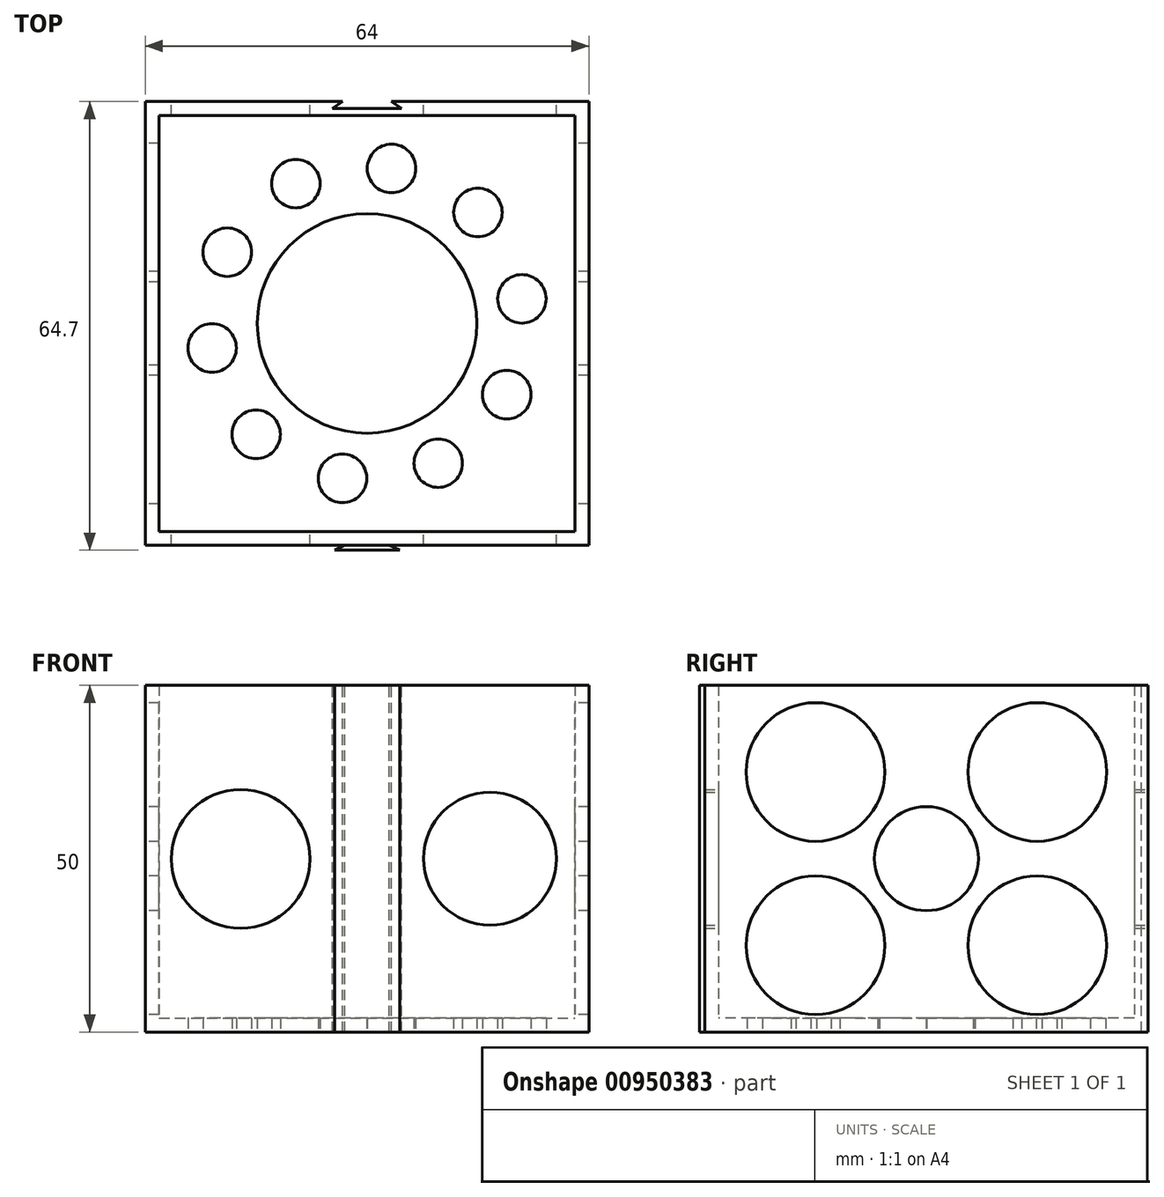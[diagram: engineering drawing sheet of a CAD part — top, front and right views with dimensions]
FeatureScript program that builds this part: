
annotation { "Feature Type Name" : "Feature", "Feature Type Description" : "" }
export const myFeature = defineFeature(function(context is Context, id is Id, definition is map)
    precondition{}
    {
        {
            var Q0;
            Q0=qCreatedBy(makeId("Top.planeOp"),FACE);
            var sketch = newSketch(context, id + "F0", { "sketchPlane" : qUnion([Q0])});
            skLineSegment(sketch, "E0.bottom", {"start": v(-32, 32) * mm, "end": v(32, 32) * mm});
            skLineSegment(sketch, "E0.top", {"start": v(-32, -32) * mm, "end": v(32, -32) * mm});
            skLineSegment(sketch, "E0.left", {"start": v(-32, 32) * mm, "end": v(-32, -32) * mm});
            skLineSegment(sketch, "E0.right", {"start": v(32, 32) * mm, "end": v(32, -32) * mm});
            skPoint(sketch, "E0.middle", {"position": v(0, 0) * mm});
            skSolve(sketch);
        }
        {
            var Q0;
            Q0=makeQuery(id+"F0.imprint","IMPRINT",FACE,{"disambiguationData":[TD([[makeQuery(id+"F0.imprint","IMPRINT",EDGE,{"derivedFrom":sQuery(id+"F0.wireOp",EDGE,"E0.bottom")}),-1.0]])]});
            extrude(context, id + "F1", {"entities" : qUnion([Q0]), "depth" : 50 * mm, "offsetDistance" : 25 * mm});
        }
        {
            var Q0;
            Q0=makeQuery(id+"F1.opExtrude","CAP_FACE",FACE,{"disambiguationData":[OSD([sQuery(id+"F0.wireOp",EDGE,"E0.bottom"),sQuery(id+"F0.wireOp",EDGE,"E0.top"),sQuery(id+"F0.wireOp",EDGE,"E0.left"),sQuery(id+"F0.wireOp",EDGE,"E0.right")])],"isStart":false});
            shell(context, id + "F2", {"entities" : qUnion([Q0]), "thickness" : 2 * mm});
        }
        {
            var Q0;
            Q0=makeQuery(id+"F1.opExtrude","CAP_FACE",FACE,{"disambiguationData":[OSD([sQuery(id+"F0.wireOp",EDGE,"E0.bottom"),sQuery(id+"F0.wireOp",EDGE,"E0.top"),sQuery(id+"F0.wireOp",EDGE,"E0.left"),sQuery(id+"F0.wireOp",EDGE,"E0.right")])],"isStart":false});
            var sketch = newSketch(context, id + "F3", { "sketchPlane" : qUnion([Q0])});
            skLineSegment(sketch, "E1", {"start": v(-3.5, 32) * mm, "end": v(0, 32) * mm});
            skLineSegment(sketch, "E2", {"start": v(0, 32) * mm, "end": v(3.5, 32) * mm});
            skLineSegment(sketch, "E3", {"start": v(-5, 31) * mm, "end": v(0, 31) * mm});
            skLineSegment(sketch, "E4", {"start": v(0, 31) * mm, "end": v(5, 31) * mm});
            skLineSegment(sketch, "E5", {"start": v(5, 31) * mm, "end": v(3.5, 32) * mm});
            skLineSegment(sketch, "E6", {"start": v(-5, 31) * mm, "end": v(-3.5, 32) * mm});
            skLineSegment(sketch, "E7", {"start": v(0, -32) * mm, "end": v(-3.2, -32) * mm});
            skLineSegment(sketch, "E8", {"start": v(0, -32) * mm, "end": v(3.2, -32) * mm});
            skLineSegment(sketch, "E9", {"start": v(3.2, -32) * mm, "end": v(4.7, -32.7) * mm});
            skLineSegment(sketch, "E10", {"start": v(4.7, -32.7) * mm, "end": v(0, -32.7) * mm});
            skLineSegment(sketch, "E11", {"start": v(0, -32.7) * mm, "end": v(-4.7, -32.7) * mm});
            skLineSegment(sketch, "E12", {"start": v(-4.7, -32.7) * mm, "end": v(-3.2, -32) * mm});
            skSolve(sketch);
        }
        {
            var Q0;
            Q0=makeQuery(id+"F3.imprint","IMPRINT",FACE,{"disambiguationData":[TD([[makeQuery(id+"F3.imprint","IMPRINT",EDGE,{"derivedFrom":sQuery(id+"F3.wireOp",EDGE,"E1")}),-1.0]])]});
            extrude(context, id + "F4", {"entities" : qUnion([Q0]), "operationType" : NewBodyOperationType.REMOVE, "oppositeDirection" : true, "depth" : 50 * mm, "offsetDistance" : 25 * mm});
        }
        {
            var Q0;
            Q0=makeQuery(id+"F3.imprint","IMPRINT",FACE,{"disambiguationData":[TD([[makeQuery(id+"F3.imprint","IMPRINT",EDGE,{"derivedFrom":sQuery(id+"F3.wireOp",EDGE,"E7")}),-1.0]])]});
            extrude(context, id + "F5", {"entities" : qUnion([Q0]), "oppositeDirection" : true, "depth" : 50 * mm, "offsetDistance" : 25 * mm});
        }
        {
            var Q0;
            Q0=makeQuery(id+"F1.opExtrude","SWEPT_FACE",FACE,{"disambiguationData":[OSD([sQuery(id+"F0.wireOp",EDGE,"E0.left")])]});
            var sketch = newSketch(context, id + "F6", { "sketchPlane" : qUnion([Q0])});
            skLineSegment(sketch, "E13", {"start": v(0, 50) * mm, "end": v(0, 0) * mm, "construction": true});
            skLineSegment(sketch, "E14", {"start": v(32, 25) * mm, "end": v(-32, 25) * mm, "construction": true});
            skLineSegment(sketch, "E15", {"start": v(32, 50) * mm, "end": v(-32, 0) * mm, "construction": true});
            skLineSegment(sketch, "E16", {"start": v(32, 0) * mm, "end": v(-32, 50) * mm, "construction": true});
            skLineSegment(sketch, "E17", {"start": v(-32, 25) * mm, "end": v(0, 50) * mm, "construction": true});
            skLineSegment(sketch, "E18", {"start": v(32, 25) * mm, "end": v(0, 50) * mm, "construction": true});
            skLineSegment(sketch, "E19", {"start": v(32, 25) * mm, "end": v(0, 0) * mm, "construction": true});
            skLineSegment(sketch, "E20", {"start": v(-32, 25) * mm, "end": v(0, 0) * mm, "construction": true});
            skCircle(sketch, "E21", {"center": v(-16, 37.5) * mm, "radius": 10 * mm});
            skCircle(sketch, "E22", {"center": v(16, 37.5) * mm, "radius": 10 * mm});
            skCircle(sketch, "E23", {"center": v(-16, 12.5) * mm, "radius": 10 * mm});
            skCircle(sketch, "E24", {"center": v(16, 12.5) * mm, "radius": 10 * mm});
            skCircle(sketch, "E25", {"center": v(0, 25) * mm, "radius": 7.5 * mm});
            skSolve(sketch);
        }
        {
            var Q0;
            Q0=makeQuery(id+"F6.imprint","IMPRINT",FACE,{"disambiguationData":[TD([[makeQuery(id+"F6.imprint","IMPRINT",EDGE,{"derivedFrom":sQuery(id+"F6.wireOp",EDGE,"E24")}),1.0]])]});
            var Q1;
            Q1=makeQuery(id+"F6.imprint","IMPRINT",FACE,{"disambiguationData":[TD([[makeQuery(id+"F6.imprint","IMPRINT",EDGE,{"derivedFrom":sQuery(id+"F6.wireOp",EDGE,"E23")}),1.0]])]});
            var Q2;
            Q2=makeQuery(id+"F6.imprint","IMPRINT",FACE,{"disambiguationData":[TD([[makeQuery(id+"F6.imprint","IMPRINT",EDGE,{"derivedFrom":sQuery(id+"F6.wireOp",EDGE,"E25")}),1.0]])]});
            var Q3;
            Q3=makeQuery(id+"F6.imprint","IMPRINT",FACE,{"disambiguationData":[TD([[makeQuery(id+"F6.imprint","IMPRINT",EDGE,{"derivedFrom":sQuery(id+"F6.wireOp",EDGE,"E22")}),1.0]])]});
            var Q4;
            Q4=makeQuery(id+"F6.imprint","IMPRINT",FACE,{"disambiguationData":[TD([[makeQuery(id+"F6.imprint","IMPRINT",EDGE,{"derivedFrom":sQuery(id+"F6.wireOp",EDGE,"E21")}),1.0]])]});
            extrude(context, id + "F7", {"entities" : qUnion([Q0, Q1, Q2, Q3, Q4]), "operationType" : NewBodyOperationType.REMOVE, "oppositeDirection" : true, "depth" : 70 * mm, "offsetDistance" : 25 * mm});
        }
        {
            var Q0;
            {var subQ0=sQuery(id+"F0.wireOp",EDGE,"E0.right");var subQ3=sQuery(id+"F0.wireOp",EDGE,"E0.bottom");Q0=makeQuery(id+"F4.boolean.opBoolean","SPLIT",FACE,{"disambiguationData":[TD([makeQuery(id+"F1.opExtrude","SWEPT_FACE",FACE,{"disambiguationData":[OSD([subQ0])]})])],"derivedFrom":makeQuery(id+"F1.opExtrude","SWEPT_FACE",FACE,{"disambiguationData":[OSD([subQ3])]})});}
            var sketch = newSketch(context, id + "F8", { "sketchPlane" : qUnion([Q0])});
            skLineSegment(sketch, "E26", {"start": v(-3.5, 50) * mm, "end": v(-32, 0) * mm, "construction": true});
            skLineSegment(sketch, "E27", {"start": v(-32, 50) * mm, "end": v(-3.5, 0) * mm, "construction": true});
            skLineSegment(sketch, "E28", {"start": v(4, 0) * mm, "end": v(32.5, 50) * mm, "construction": true});
            skLineSegment(sketch, "E29", {"start": v(-32, 25) * mm, "end": v(32.45, 25) * mm, "construction": true});
            skLineSegment(sketch, "E30", {"start": v(4, 50) * mm, "end": v(32.45, 0) * mm, "construction": true});
            skLineSegment(sketch, "E31", {"start": v(-17.75, 50) * mm, "end": v(-17.75, 0) * mm, "construction": true});
            skCircle(sketch, "E32", {"center": v(-17.75, 25) * mm, "radius": 9.6 * mm});
            skCircle(sketch, "E33", {"center": v(18.23, 24.96) * mm, "radius": 10 * mm});
            skPoint(sketch, "E33.centerSnap0", {"position": v(18.23, 25) * mm});
            skSolve(sketch);
        }
        {
            var Q0;
            Q0=makeQuery(id+"F8.imprint","IMPRINT",FACE,{"disambiguationData":[TD([[makeQuery(id+"F8.imprint","IMPRINT",EDGE,{"derivedFrom":sQuery(id+"F8.wireOp",EDGE,"E32")}),1.0]])]});
            var Q1;
            Q1=makeQuery(id+"F8.imprint","IMPRINT",FACE,{"disambiguationData":[TD([[makeQuery(id+"F8.imprint","IMPRINT",EDGE,{"derivedFrom":sQuery(id+"F8.wireOp",EDGE,"E33")}),1.0]])]});
            extrude(context, id + "F9", {"entities" : qUnion([Q0, Q1]), "operationType" : NewBodyOperationType.REMOVE, "oppositeDirection" : true, "depth" : 70 * mm, "offsetDistance" : 25 * mm});
        }
        {
            var Q0;
            Q0=makeQuery(id+"F1.opExtrude","CAP_FACE",FACE,{"disambiguationData":[OSD([sQuery(id+"F0.wireOp",EDGE,"E0.bottom"),sQuery(id+"F0.wireOp",EDGE,"E0.top"),sQuery(id+"F0.wireOp",EDGE,"E0.left"),sQuery(id+"F0.wireOp",EDGE,"E0.right")])],"isStart":true});
            var sketch = newSketch(context, id + "F10", { "sketchPlane" : qUnion([Q0])});
            skLineSegment(sketch, "E34", {"start": v(-32, 32) * mm, "end": v(32, -32) * mm, "construction": true});
            skLineSegment(sketch, "E35", {"start": v(32, 32) * mm, "end": v(-32, -32) * mm, "construction": true});
            skLineSegment(sketch, "E36", {"start": v(-32, 0) * mm, "end": v(32, 0) * mm, "construction": true});
            skLineSegment(sketch, "E37", {"start": v(32, 0) * mm, "end": v(0, 32) * mm, "construction": true});
            skLineSegment(sketch, "E38", {"start": v(0, 32) * mm, "end": v(-32, 0) * mm, "construction": true});
            skLineSegment(sketch, "E39", {"start": v(0, -31) * mm, "end": v(32, 0) * mm, "construction": true});
            skLineSegment(sketch, "E40", {"start": v(0, -31) * mm, "end": v(-32, 0) * mm, "construction": true});
            skLineSegment(sketch, "E41", {"start": v(0, 32) * mm, "end": v(0, -31) * mm, "construction": true});
            skCircle(sketch, "E42", {"center": v(-16, 16) * mm, "radius": 3.5 * mm});
            skCircle(sketch, "E43.1.0", {"center": v(-22.35, 3.54) * mm, "radius": 3.5 * mm});
            skCircle(sketch, "E43.2.0", {"center": v(-20.16, -10.27) * mm, "radius": 3.5 * mm});
            skCircle(sketch, "E43.3.0", {"center": v(-10.27, -20.16) * mm, "radius": 3.5 * mm});
            skCircle(sketch, "E43.4.0", {"center": v(3.54, -22.35) * mm, "radius": 3.5 * mm});
            skCircle(sketch, "E43.5.0", {"center": v(16, -16) * mm, "radius": 3.5 * mm});
            skCircle(sketch, "E43.6.0", {"center": v(22.35, -3.54) * mm, "radius": 3.5 * mm});
            skCircle(sketch, "E43.7.0", {"center": v(20.16, 10.27) * mm, "radius": 3.5 * mm});
            skCircle(sketch, "E43.8.0", {"center": v(10.27, 20.16) * mm, "radius": 3.5 * mm});
            skCircle(sketch, "E43.9.0", {"center": v(-3.54, 22.35) * mm, "radius": 3.5 * mm});
            skPoint(sketch, "E43.center", {"position": v(0, 0) * mm});
            skCircle(sketch, "E44", {"center": v(0, 0) * mm, "radius": 15.83 * mm});
            skSolve(sketch);
        }
        {
            var Q0;
            Q0=makeQuery(id+"F10.imprint","IMPRINT",FACE,{"disambiguationData":[TD([[makeQuery(id+"F10.imprint","IMPRINT",EDGE,{"derivedFrom":sQuery(id+"F10.wireOp",EDGE,"E42")}),1.0]])]});
            var Q1;
            Q1=makeQuery(id+"F10.imprint","IMPRINT",FACE,{"disambiguationData":[TD([[makeQuery(id+"F10.imprint","IMPRINT",EDGE,{"derivedFrom":sQuery(id+"F10.wireOp",EDGE,"E43.9.0")}),1.0]])]});
            var Q2;
            Q2=makeQuery(id+"F10.imprint","IMPRINT",FACE,{"disambiguationData":[TD([[makeQuery(id+"F10.imprint","IMPRINT",EDGE,{"derivedFrom":sQuery(id+"F10.wireOp",EDGE,"E43.8.0")}),1.0]])]});
            var Q3;
            Q3=makeQuery(id+"F10.imprint","IMPRINT",FACE,{"disambiguationData":[TD([[makeQuery(id+"F10.imprint","IMPRINT",EDGE,{"derivedFrom":sQuery(id+"F10.wireOp",EDGE,"E43.7.0")}),1.0]])]});
            var Q4;
            Q4=makeQuery(id+"F10.imprint","IMPRINT",FACE,{"disambiguationData":[TD([[makeQuery(id+"F10.imprint","IMPRINT",EDGE,{"derivedFrom":sQuery(id+"F10.wireOp",EDGE,"E43.6.0")}),1.0]])]});
            var Q5;
            Q5=makeQuery(id+"F10.imprint","IMPRINT",FACE,{"disambiguationData":[TD([[makeQuery(id+"F10.imprint","IMPRINT",EDGE,{"derivedFrom":sQuery(id+"F10.wireOp",EDGE,"E43.5.0")}),1.0]])]});
            var Q6;
            Q6=makeQuery(id+"F10.imprint","IMPRINT",FACE,{"disambiguationData":[TD([[makeQuery(id+"F10.imprint","IMPRINT",EDGE,{"derivedFrom":sQuery(id+"F10.wireOp",EDGE,"E43.4.0")}),1.0]])]});
            var Q7;
            Q7=makeQuery(id+"F10.imprint","IMPRINT",FACE,{"disambiguationData":[TD([[makeQuery(id+"F10.imprint","IMPRINT",EDGE,{"derivedFrom":sQuery(id+"F10.wireOp",EDGE,"E43.3.0")}),1.0]])]});
            var Q8;
            Q8=makeQuery(id+"F10.imprint","IMPRINT",FACE,{"disambiguationData":[TD([[makeQuery(id+"F10.imprint","IMPRINT",EDGE,{"derivedFrom":sQuery(id+"F10.wireOp",EDGE,"E43.2.0")}),1.0]])]});
            var Q9;
            Q9=makeQuery(id+"F10.imprint","IMPRINT",FACE,{"disambiguationData":[TD([[makeQuery(id+"F10.imprint","IMPRINT",EDGE,{"derivedFrom":sQuery(id+"F10.wireOp",EDGE,"E43.1.0")}),1.0]])]});
            var Q10;
            Q10=makeQuery(id+"F10.imprint","IMPRINT",FACE,{"disambiguationData":[TD([[makeQuery(id+"F10.imprint","IMPRINT",EDGE,{"derivedFrom":sQuery(id+"F10.wireOp",EDGE,"E44")}),1.0]])]});
            extrude(context, id + "F11", {"entities" : qUnion([Q0, Q1, Q2, Q3, Q4, Q5, Q6, Q7, Q8, Q9, Q10]), "operationType" : NewBodyOperationType.REMOVE, "oppositeDirection" : true, "depth" : 25 * mm, "offsetDistance" : 25 * mm});
        }
    });
